# Revit family: 40-142-411_Graa_1m_simplified
name_source: partatom
category: Generic Models
units: mm (PartAtom-declared; Revit-internal decimal feet)

## family parameters
Always vertical = Yes
Can host rebar = No
Cut with Voids When Loaded = No
Part Type = Normal
Room Calculation Point = No
Round Connector Dimension = Use Diameter
Shared = No
Work Plane-Based = No

## types (1)
- Type 1
    Artnr = 03-200-415
    Artnr_Graa_1m_simplified = 40-142-423
    Default Elevation = 0 mm  [stored 0 ft]
    Description_Graa_1m_simplified = Rutsjebane terreng 6,1 x 1,0
    Number = 20839
    Number_Graa_1m_simplified = 20839
    PartName = Montert 40-142-411
    PartName_Graa_1m_simplified = Rutsjebane terreng 6,1 x 1,0
    Revision = 0
    Revision_Graa_1m_simplified = 0

note: [stored X ft] marks values corroborated as IEEE doubles in the binary element streams (Revit-internal decimal feet)

## geometry (parser evidence)
native form markers: Sweep x11
no freeform markers — native parametric forms only
